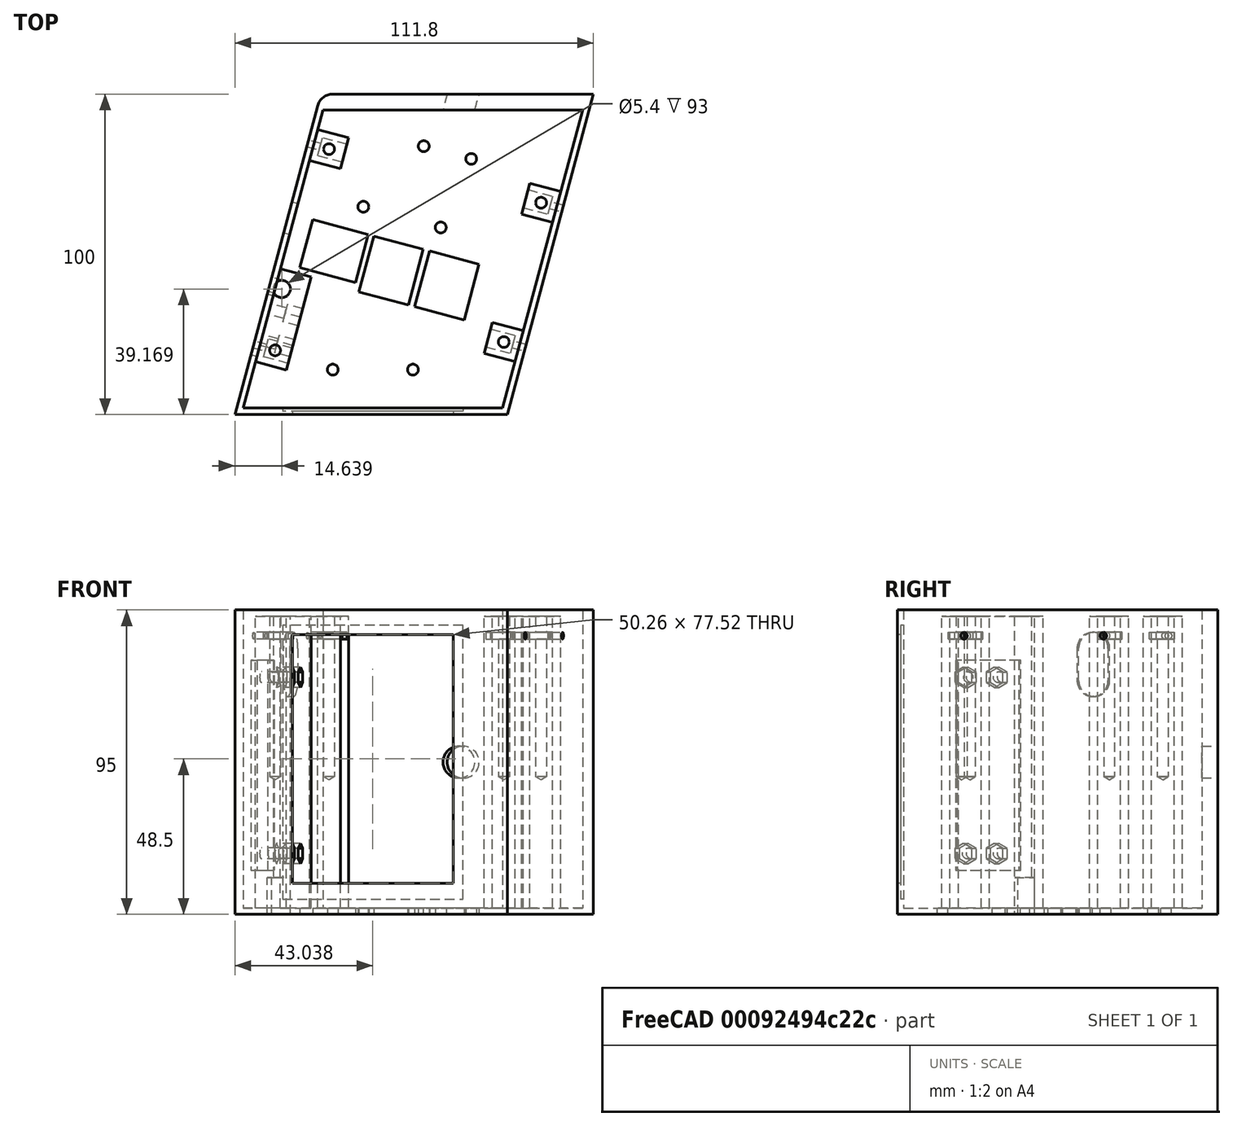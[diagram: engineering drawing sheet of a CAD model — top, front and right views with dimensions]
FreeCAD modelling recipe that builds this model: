
FCSTD DOCUMENT  (FreeCAD 0.21R33668 +26 (Git))
Label: Casing2
License: All rights reserved
LicenseURL: https://en.wikipedia.org/wiki/All_rights_reserved
objects: Sketcher::SketchObject×19, PartDesign::Pocket×14, PartDesign::CoordinateSystem×6, PartDesign::Hole×3, App::DocumentObjectGroup×3, PartDesign::Pad×2, Spreadsheet::Sheet×1, PartDesign::Fillet×1, App::FeaturePython×1, PartDesign::Body×1, App::Part×1, Mesh::Feature×1
note: 66 computed .brp shape members not serialized (recipe doc carries the construction recipe); baked Part::Feature solids carry a one-line shape summary decoded from their .brp
EXTERNAL_REF file=Display_Berrybase.FCStd obj=Spreadsheet
EXTERNAL_REF file=MLX90640.FCStd obj=Spreadsheet
EXTERNAL_REF file=Raspberrypi4B.FCStd obj=Spreadsheet
EXTERNAL_REF file=Support_Display_new.FCStd obj=Spreadsheet
EXTERNAL_REF file=Support_MLX.FCStd obj=Spreadsheet
EXTERNAL_REF file=Support_Raspi_new.FCStd obj=Spreadsheet

FEATURE [Spreadsheet::Sheet] Spreadsheet
  cells = B2='slant; C2(slant)==15 °; E2='main_case_width; F2(main_case_width)==95 mm; H2='display_width; I2(display_width)==<<Display_Berrybase>>#Spreadsheet.width; B3='walls_thickness; C3(walls_thickness)==2 mm; E3='main_case_height; F3(main_case_height)==85 mm; H3='display_height; I3(display_height)==<<Display_Berrybase>>#Spreadsheet.height; B4='screw_radius; C4(screw_radius)==1.5 mm; E4='main_case_length; F4(main_case_length)==100 mm; B5='front_thickness; C5(front_thickness)==5 mm; H5='mlx_cam_height; I5(mlx_cam_height)==<<MLX90640>>#Spreadsheet.cam_height; H6='mlx_extra_space; I6(mlx_extra_space)==2 mm; H7='mlx_radius; I7(mlx_radius)==<<MLX90640>>#Spreadsheet.cam_rad; B9='display_guard_depth; C9(display_guard_depth)==1 mm; E9='mlx_carrier_height; F9(mlx_carrier_height)==<<Support_MLX>>#Spreadsheet.carrier_height; H9='raspi_carrier_hole_dist; I9(raspi_carrier_hole_dist)==<<Support_Raspi_new>>#<<Spreadsheet>>.carrier_holes_space; B10='display_guard_size; C10(display_guard_size)==3 mm; E10='mlx_carrier_width; F10(mlx_carrier_width)==<<Support_MLX>>#Spreadsheet.carrier_width; H10='raspi_carrier_height; I10(raspi_carrier_height)==<<Support_Raspi_new>>#Spreadsheet.height; B11='display_clearance; C11(display_clearance)==1 mm; H11='raspi_carrier_depth; I11(raspi_carrier_depth)==<<Support_Raspi_new>>#Spreadsheet.depth; B12='display_hole_depth; C12(display_hole_depth)==display_width + display_clearance - display_guard_size - display_right_guard_extra; E12='beams_width; F12(beams_width)==10 mm; B13='display_right_guard_extra; C13(display_right_guard_extra)==5 mm; E13='beams_height; F13(beams_height)==10 mm; H13='raspi_height; I13(raspi_height)==<<Raspberrypi4B>>#Spreadsheet.height; H14='raspi_thickness; I14(raspi_thickness)==<<Raspberrypi4B>>#Spreadsheet.thickness; B15='display_thickness; C15(display_thickness)==<<Display_Berrybase>>#Spreadsheet.thickness; E15='beam_LB_offset; F15(beam_LB_offset)==80 mm; B16='display_carrier_height; C16(display_carrier_height)==<<Support_Display_new>>#Spreadsheet.height; E16='beam_LF_offset; F16(beam_LF_offset)==15 mm; H16='raspi_usb_width; I16(raspi_usb_width)==14 mm; E17='beam_UB_offset; F17(beam_UB_offset)==60 mm; H17='raspi_usb_height; I17(raspi_usb_height)==<<Raspberrypi4B>>#Spreadsheet.usb_height + 0 mm; B18='display_carrier_hole_dist; C18(display_carrier_hole_dist)==<<Support_Display_new>>#<<Spreadsheet>>.beams_seperation + <<Support_Display_new>>#<<Spreadsheet>>.beams_width; E18='beam_UF_offset; F18(beam_UF_offset)==15 mm; H18='raspi_eth_width; I18(raspi_eth_width)==<<Raspberrypi4B>>#Spreadsheet.ethernet_width; B19='display_carrier_offset; C19(display_carrier_offset)==display_thickness + display_carrier_height / 2 + 1 mm; H19='raspi_eth_height; I19(raspi_eth_height)==<<Raspberrypi4B>>#Spreadsheet.ethernet_height; E20='interface_width; F20(interface_width)==65 mm; H20='raspi_usb_lower_offset; I20(raspi_usb_lower_offset)==<<Raspberrypi4B>>#Spreadsheet.usb_lower_offset; B21='ports_clearance; C21(ports_clearance)==2 mm; E21='interface_height; F21(interface_height)==20 mm; H21='raspi_usb_middle_offset; I21(raspi_usb_middle_offset)==<<Raspberrypi4B>>#Spreadsheet.usb_middle_offset; E22='interface_screws_width; F22(interface_screws_width)==interface_width - beams_width; H22='raspi_eth_offset; I22(raspi_eth_offset)==<<Raspberrypi4B>>#Spreadsheet.ethernet_offset; B23='pen_radius; C23(pen_radius)==2.5 mm; E23='interface_screws_height; F23(interface_screws_height)==interface_height - beams_width; B24='pen_length; C24(pen_length)==90 mm; E24='interface_offset; F24(interface_offset)==2 mm; H24='sq_nut_width; I24(sq_nut_width)==5.8 mm; B25='pen_grip_width; C25(pen_grip_width)==7.5 mm; E25='interface_clearance; F25(interface_clearance)==0.5 mm; H25='sq_nut_height; I25(sq_nut_height)==2.1 mm; B26='pen_grip_height; C26(pen_grip_height)==11.5 mm; H26='sq_nut_hole_depth; I26(sq_nut_hole_depth)==(beams_height + sq_nut_width) / 2; B27='pen_radius_tolerance; C27(pen_radius_tolerance)==0.2 mm; H27='sq_nut_hole_offset; I27(sq_nut_hole_offset)==5 mm; B28='pen_hole_offset; C28(pen_hole_offset)==pen_grip_width - pen_radius - 1 mm
FEATURE [Sketcher::SketchObject] Sketch
  FullyConstrained = true
  MapMode = 5
  Support = -> [XY_Plane]
  expr: Constraints[7] = 90 ° + Spreadsheet.slant
  expr: Constraints[8] = Spreadsheet.main_case_height
  expr: Constraints[9] = Spreadsheet.main_case_length
  sketch-geometry (4):
    g0: LineSegment StartX=-29.1025 StartY=50 StartZ=0 EndX=55.8975 EndY=50 EndZ=0
    g1: LineSegment StartX=55.8975 StartY=50 StartZ=0 EndX=29.1025 EndY=-50 EndZ=0
    g2: LineSegment StartX=29.1025 StartY=-50 StartZ=0 EndX=-55.8975 EndY=-50 EndZ=0
    g3: LineSegment StartX=-55.8975 StartY=-50 StartZ=0 EndX=-29.1025 EndY=50 EndZ=0
  constraints (10):
    c: Coincident(g0,g1)
    c: Coincident(g1,g2)
    c: Coincident(g2,g3)
    c: Coincident(g3,g0)
    c: Horizontal(g0)
    c: Symmetric(g0,g2,g-1)
    c: Symmetric(g0,g1,g-1)
    c: Angle(g1,g2) = 1.8326
    c: DistanceX(g2,g2) = 85
    c: DistanceY(g1,g1) = 100
FEATURE [PartDesign::Pad] Pad
  Direction = (0,0,1)
  Length = 95
  Length2 = 10
  Profile = -> Sketch
  ReferenceAxis = -> Sketch [N_Axis]
  Type = 0
  expr: Length = Spreadsheet.main_case_width
FEATURE [Sketcher::SketchObject] Sketch001
  ExternalGeometry = -> [Pad]
  FullyConstrained = true
  MapMode = 5
  Placement = pos=(0,0,95) rot=(0,0,1;0rad)
  Support = -> [Pad]
  expr: Constraints[4] = Spreadsheet.walls_thickness
  expr: Constraints[5] = Spreadsheet.walls_thickness * (1 - tan(Spreadsheet.slant))
  expr: Constraints[7] = Spreadsheet.main_case_height - Spreadsheet.walls_thickness * 2
  expr: Constraints[8] = Spreadsheet.front_thickness
  sketch-geometry (4):
    g0: LineSegment StartX=-28.4423 StartY=45 StartZ=0 EndX=52.5577 EndY=45 EndZ=0
    g1: LineSegment StartX=52.5577 StartY=45 StartZ=0 EndX=27.6384 EndY=-48 EndZ=0
    g2: LineSegment StartX=27.6384 StartY=-48 StartZ=0 EndX=-53.3616 EndY=-48 EndZ=0
    g3: LineSegment StartX=-53.3616 StartY=-48 StartZ=0 EndX=-28.4423 EndY=45 EndZ=0
  constraints (12):
    c: Coincident(g0,g1)
    c: Coincident(g1,g2)
    c: Coincident(g2,g3)
    c: Coincident(g3,g0)
    c: DistanceY(g-5,g2) = 2
    c: DistanceX(g1,g-6) = 1.4641
    c: Horizontal(g2)
    c: DistanceX(g2,g2) = 81
    c: DistanceY(g0,g-4) = 5
    c: Horizontal(g0)
    c: Parallel(g3,g-4)
    c: Parallel(g1,g-6)
FEATURE [PartDesign::Pocket] Pocket
  BaseFeature = -> Pad
  Direction = (0,0,-1)
  Length = 93
  Length2 = 5
  Profile = -> Sketch001
  ReferenceAxis = -> Sketch001 [N_Axis]
  Type = 0
  expr: Length = Spreadsheet.main_case_width - Spreadsheet.walls_thickness
FEATURE [Sketcher::SketchObject] Sketch002
  ExternalGeometry = -> [Pocket]
  FullyConstrained = true
  MapMode = 5
  Placement = pos=(0,-48,0) rot=(0,0.707107,0.707107;3.14159rad)
  Support = -> [Pocket]
  expr: Constraints[11] = (Spreadsheet.main_case_width - Spreadsheet.walls_thickness * 2) / 2
  expr: Constraints[13] = Spreadsheet.display_width + Spreadsheet.display_clearance
  expr: Constraints[14] = Spreadsheet.display_height + Spreadsheet.display_clearance
  sketch-geometry (6):
    g0: LineSegment StartX=40.9916 StartY=4.74 StartZ=0 EndX=-15.2684 EndY=4.74 EndZ=0
    g1: LineSegment StartX=-15.2684 StartY=4.74 StartZ=0 EndX=-15.2684 EndY=90.26 EndZ=0
    g2: LineSegment StartX=-15.2684 StartY=90.26 StartZ=0 EndX=40.9916 EndY=90.26 EndZ=0
    g3: LineSegment StartX=40.9916 StartY=90.26 StartZ=0 EndX=40.9916 EndY=4.74 EndZ=0
    g4: LineSegment StartX=12.8616 StartY=95 StartZ=0 EndX=12.8616 EndY=2 EndZ=0
    g5: GeomPoint X=12.8616 Y=47.5 Z=0
  constraints (15):
    c: Coincident(g0,g1)
    c: Coincident(g1,g2)
    c: Coincident(g2,g3)
    c: Coincident(g3,g0)
    c: Horizontal(g0)
    c: Horizontal(g2)
    c: Vertical(g1)
    c: Vertical(g3)
    c: Symmetric(g-6,g-6,g4)
    c: Symmetric(g-5,g-4,g4)
    c: PointOnObject(g5,g4)
    c: DistanceY(g4,g5) = 45.5
    c: Symmetric(g1,g0,g5)
    c: DistanceY(g1,g1) = 85.52
    c: DistanceX(g2,g2) = 56.26
FEATURE [PartDesign::Pocket] Pocket001
  BaseFeature = -> Pocket
  Direction = (0,-1,2e-16)
  Length = 1
  Length2 = 5
  Profile = -> Sketch002
  ReferenceAxis = -> Sketch002 [N_Axis]
  Type = 0
  expr: Length = Spreadsheet.walls_thickness - Spreadsheet.display_guard_depth
FEATURE [Sketcher::SketchObject] Sketch003
  ExternalGeometry = -> [Pocket001]
  FullyConstrained = true
  MapMode = 5
  Placement = pos=(0,-49,1.23e-14) rot=(0,0.707107,0.707107;3.14159rad)
  Support = -> [Pocket001]
  expr: Constraints[10] = Spreadsheet.display_guard_size
  expr: Constraints[11] = Spreadsheet.display_guard_size
  expr: Constraints[8] = Spreadsheet.display_right_guard_extra
  expr: Constraints[9] = Spreadsheet.display_guard_size
  sketch-geometry (4):
    g0: LineSegment StartX=-12.2684 StartY=87.26 StartZ=0 EndX=37.9916 EndY=87.26 EndZ=0
    g1: LineSegment StartX=37.9916 StartY=87.26 StartZ=0 EndX=37.9916 EndY=9.74 EndZ=0
    g2: LineSegment StartX=37.9916 StartY=9.74 StartZ=0 EndX=-12.2684 EndY=9.74 EndZ=0
    g3: LineSegment StartX=-12.2684 StartY=9.74 StartZ=0 EndX=-12.2684 EndY=87.26 EndZ=0
  constraints (12):
    c: Coincident(g0,g1)
    c: Coincident(g1,g2)
    c: Coincident(g2,g3)
    c: Coincident(g3,g0)
    c: Horizontal(g0)
    c: Horizontal(g2)
    c: Vertical(g1)
    c: Vertical(g3)
    c: DistanceY(g-5,g2) = 5
    c: DistanceY(g0,g-5) = 3
    c: DistanceX(g-5,g0) = 3
    c: DistanceX(g0,g-4) = 3
FEATURE [PartDesign::Pocket] Pocket002
  BaseFeature = -> Pocket001
  Direction = (0,-1,2e-16)
  Length = 1
  Length2 = 5
  Profile = -> Sketch003
  ReferenceAxis = -> Sketch003 [N_Axis]
  Type = 0
  expr: Length = Spreadsheet.display_guard_depth
FEATURE [PartDesign::Fillet] Fillet
  Base = -> Pocket002 [Edge1]
  BaseFeature = -> Pocket002
  Radius = 5
  SupportTransform = false
  UseAllEdges = false
FEATURE [Sketcher::SketchObject] Sketch004
  ExternalGeometry = -> [Fillet]
  FullyConstrained = true
  MapMode = 5
  Placement = pos=(0,0,2) rot=(0,0,1;0rad)
  Support = -> [Fillet]
  expr: Constraints[10] = Spreadsheet.display_carrier_offset
  expr: Constraints[11] = Spreadsheet.display_carrier_hole_dist
  expr: Constraints[12] = Spreadsheet.screw_radius
  expr: Constraints[13] = Spreadsheet.screw_radius
  expr: Constraints[14] = Spreadsheet.screw_radius
  expr: Constraints[15] = Spreadsheet.screw_radius
  expr: Constraints[21] = Spreadsheet.raspi_carrier_height
  expr: Constraints[22] = Spreadsheet.walls_thickness
  expr: Constraints[25] = Spreadsheet.raspi_carrier_hole_dist
  expr: Constraints[26] = Spreadsheet.screw_radius
  expr: Constraints[27] = Spreadsheet.screw_radius
  expr: Constraints[30] = Spreadsheet.mlx_carrier_height - Spreadsheet.mlx_carrier_width
  expr: Constraints[33] = 90 ° + Spreadsheet.slant
  expr: Constraints[9] = Spreadsheet.mlx_cam_height + Spreadsheet.mlx_extra_space + Spreadsheet.front_thickness
  sketch-geometry (14):
    g0: Circle CenterX=3.02671 CenterY=33.7326 CenterZ=0 NormalX=0 NormalY=0 NormalZ=1 AngleXU=0 Radius=1.5
    g1: Circle CenterX=17.8247 CenterY=29.7674 CenterZ=0 NormalX=0 NormalY=0 NormalZ=1 AngleXU=0 Radius=1.5
    g2: Circle CenterX=-15.8225 CenterY=14.8236 CenterZ=0 NormalX=0 NormalY=0 NormalZ=1 AngleXU=0 Radius=1.5
    g3: Circle CenterX=8.32565 CenterY=8.35314 CenterZ=0 NormalX=0 NormalY=0 NormalZ=1 AngleXU=0 Radius=1.5
    g4: Circle CenterX=-25.3616 CenterY=-36 CenterZ=0 NormalX=0 NormalY=0 NormalZ=1 AngleXU=0 Radius=1.5
    g5: Circle CenterX=-0.361561 CenterY=-36 CenterZ=0 NormalX=0 NormalY=0 NormalZ=1 AngleXU=0 Radius=1.5
    g6: LineSegment StartX=15.3158 StartY=50 StartZ=0 EndX=10.4257 EndY=31.75 EndZ=0
    g7: LineSegment StartX=3.02671 StartY=33.7326 StartZ=0 EndX=17.8247 EndY=29.7674 EndZ=0
    g8: LineSegment StartX=-12.8616 StartY=-48 StartZ=0 EndX=-12.8616 EndY=-36 EndZ=0
    g9: LineSegment StartX=-25.3616 StartY=-36 StartZ=0 EndX=-0.361561 EndY=-36 EndZ=0
    g10: LineSegment StartX=-35.141 StartY=20 StartZ=0 EndX=25.7123 EndY=3.6944 EndZ=0
    g11: GeomPoint X=-33.2092 Y=19.4824 Z=0
    g12: GeomPoint X=-3.74843 Y=11.5884 Z=0
    g13: LineSegment StartX=-25.2659 StartY=50 StartZ=0 EndX=55.8975 EndY=50 EndZ=0
  constraints (34):
    c: Symmetric(g7,g7,g6)
    c: Coincident(g0,g7)
    c: Coincident(g1,g7)
    c: Symmetric(g-5,g-6,g8)
    c: Symmetric(g9,g9,g8)
    c: Coincident(g4,g9)
    c: Coincident(g5,g9)
    c: Vertical(g8)
    c: Horizontal(g9)
    c: DistanceY(g6,g6) = 18.25
    c: DistanceY(g8,g8) = 12
    c: DistanceX(g9,g9) = 25
    c: Radius(g0) = 1.5
    c: Radius(g1) = 1.5
    c: Radius(g4) = 1.5
    c: Radius(g5) = 1.5
    c: PointOnObject(g10,g-4)
    c: PointOnObject(g11,g10)
    c: Symmetric(g11,g10,g12)
    c: Perpendicular(g10,g-4)
    c: DistanceY(g10,g-4) = 25
    c: Distance(g11,g10) = 61
    c: Distance(g11,g10) = 2
    c: Symmetric(g2,g3,g12)
    c: PointOnObject(g2,g10)
    c: Distance(g3,g2) = 25
    c: Radius(g2) = 1.5
    c: Radius(g3) = 1.5
    c: Symmetric(g-7,g-8,g6)
    c: Perpendicular(g7,g6)
    c: Distance(g7) = 15.32
    c: Coincident(g13,g-7)
    c: Coincident(g13,g-8)
    c: Angle(g6,g13) = 1.8326
FEATURE [PartDesign::Hole] Hole
  BaseFeature = -> Fillet
  CustomThreadClearance = 0
  Depth = 358.646
  DepthType = 1
  Diameter = 3.4
  DrillForDepth = false
  DrillPoint = 1
  DrillPointAngle = 118
  HoleCutCountersinkAngle = 90
  HoleCutCustomValues = false
  HoleCutDepth = 0
  HoleCutDiameter = 6.1
  HoleCutType = 0
  ModelThread = false
  Profile = -> Sketch004
  Tapered = false
  TaperedAngle = 90
  ThreadClass = 0
  ThreadDepth = 358.646
  ThreadDepthType = 0
  ThreadDirection = 0
  ThreadFit = 0
  ThreadSize = 9
  ThreadType = 1
  Threaded = false
  UseCustomThreadClearance = false
FEATURE [Sketcher::SketchObject] Sketch005
  ExternalGeometry = -> [Hole]
  FullyConstrained = true
  MapMode = 5
  Placement = pos=(0,50,0) rot=(0,0.707107,0.707107;3.14159rad)
  Support = -> [Hole]
  expr: Constraints[2] = (Spreadsheet.mlx_radius + 0.15 mm) / cos(Spreadsheet.slant)
  sketch-geometry (3):
    g0: LineSegment StartX=-55.8975 StartY=95 StartZ=0 EndX=25.2659 EndY=0 EndZ=0
    g1: LineSegment StartX=-55.8975 StartY=0 StartZ=0 EndX=25.2659 EndY=95 EndZ=0
    g2: Circle CenterX=-15.3158 CenterY=47.5 CenterZ=0 NormalX=0 NormalY=0 NormalZ=1 AngleXU=0 Radius=4.96933
  constraints (7):
    c: PointOnObject(g2,g0)
    c: PointOnObject(g2,g1)
    c: Radius(g2) = 4.96933
    c: Coincident(g0,g-3)
    c: Coincident(g1,g-4)
    c: Coincident(g0,g-4)
    c: Coincident(g1,g-3)
FEATURE [PartDesign::Pocket] Pocket003
  BaseFeature = -> Hole
  Direction = (-0.267949,-1,0)
  Length = 5
  Length2 = 5
  Profile = -> Sketch005
  ReferenceAxis = -> Sketch005 [N_Axis]
  Type = 0
  UseCustomVector = true
  expr: .Direction.x = tan(Spreadsheet.slant) * -1
  expr: Length = Spreadsheet.front_thickness
FEATURE [Sketcher::SketchObject] Sketch006
  ExternalGeometry = -> [Pocket003]
  FullyConstrained = true
  MapMode = 5
  Placement = pos=(0,0,2) rot=(0,0,1;0rad)
  Support = -> [Pocket003]
  expr: Constraints[14] = Spreadsheet.raspi_height
  expr: Constraints[15] = Spreadsheet.raspi_thickness
  expr: Constraints[19] = Spreadsheet.raspi_eth_offset
  expr: Constraints[20] = Spreadsheet.raspi_usb_middle_offset
  expr: Constraints[21] = Spreadsheet.raspi_usb_lower_offset
  expr: Constraints[49] = Spreadsheet.raspi_eth_width + Spreadsheet.ports_clearance
  expr: Constraints[4] = (Spreadsheet.raspi_carrier_depth - Spreadsheet.ports_clearance) / 2
  expr: Constraints[50] = Spreadsheet.raspi_usb_width + Spreadsheet.ports_clearance
  expr: Constraints[51] = Spreadsheet.raspi_usb_width + Spreadsheet.ports_clearance
  expr: Constraints[52] = Spreadsheet.raspi_eth_height + Spreadsheet.ports_clearance
  expr: Constraints[53] = Spreadsheet.raspi_usb_height + Spreadsheet.ports_clearance
  expr: Constraints[54] = Spreadsheet.raspi_usb_height + Spreadsheet.ports_clearance
  sketch-geometry (21):
    g0: LineSegment StartX=-15.8225 StartY=14.8236 StartZ=0 EndX=8.32565 EndY=8.35314 EndZ=0
    g1: LineSegment StartX=-3.74843 StartY=11.5884 StartZ=0 EndX=-4.7837 EndY=7.72468 EndZ=0
    g2: LineSegment StartX=22.2622 StartY=0.477744 StartZ=0 EndX=-31.8296 EndY=14.9716 EndZ=0
    g3: LineSegment StartX=-31.8296 StartY=14.9716 StartZ=0 EndX=-32.8649 EndY=11.1079 EndZ=0
    g4: LineSegment StartX=-32.8649 StartY=11.1079 StartZ=0 EndX=21.2269 EndY=-3.38596 EndZ=0
    g5: LineSegment StartX=21.2269 StartY=-3.38596 StartZ=0 EndX=22.2622 EndY=0.477744 EndZ=0
    g6: GeomPoint X=-22.9642 Y=8.45501 Z=0
    g7: GeomPoint X=-4.85305 Y=3.60216 Z=0
    g8: GeomPoint X=12.5336 Y=-1.05659 Z=0
    g9: LineSegment StartX=-31.6575 StartY=10.7844 StartZ=0 EndX=-14.2708 EndY=6.12564 EndZ=0
    g10: LineSegment StartX=-14.2708 StartY=6.12564 StartZ=0 EndX=-18.2825 EndY=-8.84621 EndZ=0
    g11: LineSegment StartX=-18.2825 StartY=-8.84621 StartZ=0 EndX=-35.6692 EndY=-4.18747 EndZ=0
    g12: LineSegment StartX=-35.6692 StartY=-4.18747 StartZ=0 EndX=-31.6575 EndY=10.7844 EndZ=0
    g13: LineSegment StartX=-12.5805 StartY=5.67271 StartZ=0 EndX=2.87435 EndY=1.5316 EndZ=0
    g14: LineSegment StartX=2.87435 StartY=1.5316 StartZ=0 EndX=-1.78439 EndY=-15.8551 EndZ=0
    g15: LineSegment StartX=-1.78439 StartY=-15.8551 StartZ=0 EndX=-17.2392 EndY=-11.714 EndZ=0
    g16: LineSegment StartX=-17.2392 StartY=-11.714 StartZ=0 EndX=-12.5805 EndY=5.67271 EndZ=0
    g17: LineSegment StartX=4.8062 StartY=1.01396 StartZ=0 EndX=20.261 EndY=-3.12714 EndZ=0
    g18: LineSegment StartX=20.261 StartY=-3.12714 StartZ=0 EndX=15.6023 EndY=-20.5138 EndZ=0
    g19: LineSegment StartX=15.6023 StartY=-20.5138 StartZ=0 EndX=0.147462 EndY=-16.3727 EndZ=0
    g20: LineSegment StartX=0.147462 StartY=-16.3727 StartZ=0 EndX=4.8062 EndY=1.01396 EndZ=0
  constraints (55):
    c: Coincident(g0,g-3)
    c: Coincident(g0,g-4)
    c: Symmetric(g0,g0,g1)
    c: Perpendicular(g1,g0)
    c: Distance(g1) = 4
    c: Coincident(g2,g3)
    c: Coincident(g3,g4)
    c: Coincident(g4,g5)
    c: Coincident(g5,g2)
    c: Symmetric(g2,g2,g1)
    c: Parallel(g0,g2)
    c: Parallel(g2,g4)
    c: Parallel(g1,g5)
    c: Parallel(g1,g3)
    c: Distance(g2) = 56
    c: Distance(g5) = 4
    c: PointOnObject(g6,g4)
    c: PointOnObject(g7,g4)
    c: PointOnObject(g8,g4)
    c: Distance(g6,g3) = 10.25
    c: Distance(g7,g3) = 29
    c: Distance(g8,g3) = 47
    c: Coincident(g9,g10)
    c: Coincident(g10,g11)
    c: Coincident(g11,g12)
    c: Coincident(g12,g9)
    c: Coincident(g13,g14)
    c: Coincident(g14,g15)
    c: Coincident(g15,g16)
    c: Coincident(g16,g13)
    c: Coincident(g17,g18)
    c: Coincident(g18,g19)
    c: Coincident(g19,g20)
    c: Coincident(g20,g17)
    c: PointOnObject(g9,g4)
    c: PointOnObject(g13,g4)
    c: PointOnObject(g17,g4)
    c: Symmetric(g9,g9,g6)
    c: Symmetric(g13,g13,g7)
    c: Symmetric(g17,g17,g8)
    c: Equal(g9,g11)
    c: Equal(g13,g15)
    c: Equal(g17,g19)
    c: Perpendicular(g12,g9)
    c: Perpendicular(g16,g13)
    c: Perpendicular(g20,g17)
    c: Parallel(g9,g11)
    c: Parallel(g13,g15)
    c: Parallel(g17,g19)
    c: Distance(g11) = 18
    c: Distance(g15) = 16
    c: Distance(g19) = 16
    c: Distance(g12) = 15.5
    c: Distance(g16) = 18
    c: Distance(g20) = 18
FEATURE [PartDesign::Pocket] Pocket004
  BaseFeature = -> Pocket003
  Direction = (0,0,-1)
  Length = 5
  Length2 = 5
  Profile = -> Sketch006
  ReferenceAxis = -> Sketch006 [N_Axis]
  Type = 1
FEATURE [Sketcher::SketchObject] Sketch007
  ExternalGeometry = -> [Pocket004]
  FullyConstrained = true
  MapMode = 5
  Placement = pos=(0,0,2) rot=(0,0,1;0rad)
  Support = -> [Pocket004]
  expr: Constraints[36] = Spreadsheet.beams_height
  expr: Constraints[37] = Spreadsheet.beams_height
  expr: Constraints[38] = Spreadsheet.beams_height
  expr: Constraints[39] = Spreadsheet.beams_height
  expr: Constraints[40] = Spreadsheet.beams_width
  expr: Constraints[41] = Spreadsheet.beams_width * 3
  expr: Constraints[42] = Spreadsheet.beams_width
  expr: Constraints[43] = Spreadsheet.beams_width
  expr: Constraints[44] = Spreadsheet.beam_LF_offset
  expr: Constraints[45] = Spreadsheet.beam_LB_offset
  expr: Constraints[46] = Spreadsheet.beam_UF_offset
  expr: Constraints[47] = Spreadsheet.beam_UB_offset
  sketch-geometry (16):
    g0: LineSegment StartX=-30.0678 StartY=38.9333 StartZ=0 EndX=-20.4086 EndY=36.3451 EndZ=0
    g1: LineSegment StartX=-20.4086 StartY=36.3451 StartZ=0 EndX=-22.9968 EndY=26.6859 EndZ=0
    g2: LineSegment StartX=-22.9968 StartY=26.6859 StartZ=0 EndX=-32.656 EndY=29.2741 EndZ=0
    g3: LineSegment StartX=-32.656 StartY=29.2741 StartZ=0 EndX=-30.0678 EndY=38.9333 EndZ=0
    g4: LineSegment StartX=-41.7147 StartY=-4.53334 StartZ=0 EndX=-32.0554 EndY=-7.12153 EndZ=0
    g5: LineSegment StartX=-32.0554 StartY=-7.12153 StartZ=0 EndX=-39.82 EndY=-36.0993 EndZ=0
    g6: LineSegment StartX=-39.82 StartY=-36.0993 StartZ=0 EndX=-49.4793 EndY=-33.5111 EndZ=0
    g7: LineSegment StartX=-49.4793 StartY=-33.5111 StartZ=0 EndX=-41.7147 EndY=-4.53334 EndZ=0
    g8: LineSegment StartX=24.4497 StartY=-21.2637 StartZ=0 EndX=34.1089 EndY=-23.8519 EndZ=0
    g9: LineSegment StartX=34.1089 StartY=-23.8519 StartZ=0 EndX=31.5207 EndY=-33.5111 EndZ=0
    g10: LineSegment StartX=31.5207 StartY=-33.5111 StartZ=0 EndX=21.8615 EndY=-30.9229 EndZ=0
    g11: LineSegment StartX=21.8615 StartY=-30.9229 StartZ=0 EndX=24.4497 EndY=-21.2637 EndZ=0
    g12: LineSegment StartX=36.0965 StartY=22.203 StartZ=0 EndX=45.7558 EndY=19.6148 EndZ=0
    g13: LineSegment StartX=45.7558 StartY=19.6148 StartZ=0 EndX=43.1676 EndY=9.95555 EndZ=0
    g14: LineSegment StartX=43.1676 StartY=9.95555 StartZ=0 EndX=33.5083 EndY=12.5437 EndZ=0
    g15: LineSegment StartX=33.5083 StartY=12.5437 StartZ=0 EndX=36.0965 EndY=22.203 EndZ=0
  constraints (48):
    c: Coincident(g0,g1)
    c: Coincident(g1,g2)
    c: Coincident(g2,g3)
    c: Coincident(g3,g0)
    c: Coincident(g4,g5)
    c: Coincident(g5,g6)
    c: Coincident(g6,g7)
    c: Coincident(g7,g4)
    c: Coincident(g8,g9)
    c: Coincident(g9,g10)
    c: Coincident(g10,g11)
    c: Coincident(g11,g8)
    c: Coincident(g12,g13)
    c: Coincident(g13,g14)
    c: Coincident(g14,g15)
    c: Coincident(g15,g12)
    c: PointOnObject(g0,g-3)
    c: PointOnObject(g2,g-3)
    c: PointOnObject(g4,g-3)
    c: PointOnObject(g6,g-3)
    c: PointOnObject(g12,g-4)
    c: PointOnObject(g13,g-4)
    c: PointOnObject(g8,g-4)
    c: PointOnObject(g9,g-4)
    c: Equal(g3,g1)
    c: Equal(g7,g5)
    c: Equal(g13,g15)
    c: Equal(g9,g11)
    c: Parallel(g3,g1)
    c: Parallel(g7,g5)
    c: Parallel(g9,g11)
    c: Parallel(g13,g15)
    c: Perpendicular(g0,g3)
    c: Perpendicular(g4,g7)
    c: Perpendicular(g12,g13)
    c: Perpendicular(g8,g9)
    c: Distance(g0) = 10
    c: Distance(g4) = 10
    c: Distance(g12) = 10
    c: Distance(g8) = 10
    c: Distance(g1) = 10
    c: Distance(g5) = 30
    c: Distance(g15) = 10
    c: Distance(g11) = 10
    c: Distance(g6,g-6) = 15
    c: Distance(g2,g-6) = 80
    c: Distance(g9,g-6) = 15
    c: Distance(g13,g-6) = 60
FEATURE [PartDesign::Pad] Pad001
  BaseFeature = -> Pocket004
  Direction = (0,0,1)
  Length = 91
  Length2 = 10
  Profile = -> Sketch007
  ReferenceAxis = -> Sketch007 [N_Axis]
  Type = 0
  expr: Length = Spreadsheet.main_case_width - Spreadsheet.walls_thickness * 2
FEATURE [Sketcher::SketchObject] Sketch008
  ExternalGeometry = -> [Pad001]
  FullyConstrained = true
  MapMode = 5
  Placement = pos=(0,0,93) rot=(0,0,1;0rad)
  Support = -> [Pad001]
  expr: Constraints[10] = Spreadsheet.beams_width
  expr: Constraints[3] = Spreadsheet.screw_radius
  expr: Constraints[4] = Spreadsheet.screw_radius
  expr: Constraints[5] = Spreadsheet.screw_radius
  expr: Constraints[6] = Spreadsheet.screw_radius
  sketch-geometry (5):
    g0: Circle CenterX=-26.5323 CenterY=32.8096 CenterZ=0 NormalX=0 NormalY=0 NormalZ=1 AngleXU=0 Radius=1.5
    g1: Circle CenterX=39.632 CenterY=16.0793 CenterZ=0 NormalX=0 NormalY=0 NormalZ=1 AngleXU=0 Radius=1.5
    g2: Circle CenterX=27.9852 CenterY=-27.3874 CenterZ=0 NormalX=0 NormalY=0 NormalZ=1 AngleXU=0 Radius=1.5
    g3: Circle CenterX=-43.3556 CenterY=-29.9756 CenterZ=0 NormalX=0 NormalY=0 NormalZ=1 AngleXU=0 Radius=1.5
    g4: LineSegment StartX=-37.2318 StartY=-26.44 StartZ=0 EndX=-46.8911 EndY=-23.8519 EndZ=0
  constraints (12):
    c: Symmetric(g-3,g-5,g0)
    c: Symmetric(g-7,g-8,g1)
    c: Symmetric(g-10,g-11,g2)
    c: Radius(g0) = 1.5
    c: Radius(g3) = 1.5
    c: Radius(g1) = 1.5
    c: Radius(g2) = 1.5
    c: PointOnObject(g4,g-13)
    c: PointOnObject(g4,g-15)
    c: Parallel(g4,g-14)
    c: Distance(g4,g-14) = 10
    c: Symmetric(g4,g-14,g3)
FEATURE [PartDesign::Hole] Hole001
  BaseFeature = -> Pad001
  CustomThreadClearance = 0
  Depth = 50
  DepthType = 0
  Diameter = 3.4
  DrillForDepth = false
  DrillPoint = 1
  DrillPointAngle = 118
  HoleCutCountersinkAngle = 90
  HoleCutCustomValues = false
  HoleCutDepth = 0
  HoleCutDiameter = 6.1
  HoleCutType = 0
  ModelThread = false
  Profile = -> Sketch008
  Tapered = false
  TaperedAngle = 90
  ThreadClass = 0
  ThreadDepth = 50
  ThreadDepthType = 0
  ThreadDirection = 0
  ThreadFit = 0
  ThreadSize = 9
  ThreadType = 1
  Threaded = false
  UseCustomThreadClearance = false
  expr: Depth = 50
FEATURE [Sketcher::SketchObject] Sketch009
  ExternalGeometry = -> [Hole001]
  FullyConstrained = true
  MapMode = 5
  Placement = pos=(28.1278,-7.53681,0) rot=(-0.476905,0.621515,0.621515;4.0316rad)
  Support = -> [Hole001]
  expr: Constraints[19] = Spreadsheet.sq_nut_hole_offset
  expr: Constraints[20] = Spreadsheet.sq_nut_height
  expr: Constraints[21] = Spreadsheet.sq_nut_width
  expr: Constraints[25] = Spreadsheet.sq_nut_hole_offset
  expr: Constraints[26] = Spreadsheet.sq_nut_height
  expr: Constraints[27] = Spreadsheet.sq_nut_width
  sketch-geometry (10):
    g0: LineSegment StartX=-28.6889 StartY=88 StartZ=0 EndX=-22.8889 EndY=88 EndZ=0
    g1: LineSegment StartX=-22.8889 StartY=88 StartZ=0 EndX=-22.8889 EndY=85.9 EndZ=0
    g2: LineSegment StartX=-22.8889 StartY=85.9 StartZ=0 EndX=-28.6889 EndY=85.9 EndZ=0
    g3: LineSegment StartX=-28.6889 StartY=85.9 StartZ=0 EndX=-28.6889 EndY=88 EndZ=0
    g4: LineSegment StartX=16.3111 StartY=88 StartZ=0 EndX=22.1111 EndY=88 EndZ=0
    g5: LineSegment StartX=22.1111 StartY=88 StartZ=0 EndX=22.1111 EndY=85.9 EndZ=0
    g6: LineSegment StartX=22.1111 StartY=85.9 StartZ=0 EndX=16.3111 EndY=85.9 EndZ=0
    g7: LineSegment StartX=16.3111 StartY=85.9 StartZ=0 EndX=16.3111 EndY=88 EndZ=0
    g8: LineSegment StartX=-25.7889 StartY=93 StartZ=0 EndX=-25.7889 EndY=88 EndZ=0
    g9: LineSegment StartX=19.2111 StartY=93 StartZ=0 EndX=19.2111 EndY=88 EndZ=0
  constraints (28):
    c: Coincident(g0,g1)
    c: Coincident(g1,g2)
    c: Coincident(g2,g3)
    c: Coincident(g3,g0)
    c: Horizontal(g0)
    c: Horizontal(g2)
    c: Vertical(g1)
    c: Vertical(g3)
    c: Coincident(g4,g5)
    c: Coincident(g5,g6)
    c: Coincident(g6,g7)
    c: Coincident(g7,g4)
    c: Horizontal(g4)
    c: Horizontal(g6)
    c: Vertical(g5)
    c: Vertical(g7)
    c: Vertical(g8)
    c: Symmetric(g-4,g-5,g8)
    c: Symmetric(g0,g0,g8)
    c: DistanceY(g8,g8) = 5
    c: DistanceY(g3,g3) = 2.1
    c: DistanceX(g2,g2) = 5.8
    c: Vertical(g9)
    c: Symmetric(g-7,g-8,g9)
    c: Symmetric(g4,g4,g9)
    c: DistanceY(g9,g9) = 5
    c: DistanceY(g7,g7) = 2.1
    c: DistanceX(g6,g6) = 5.8
FEATURE [PartDesign::Pocket] Pocket005
  BaseFeature = -> Hole001
  Direction = (0.965926,-0.258819,-2e-16)
  Length = 7.9
  Length2 = 5
  Profile = -> Sketch009
  ReferenceAxis = -> Sketch009 [N_Axis]
  Type = 0
  expr: Length = Spreadsheet.sq_nut_hole_depth
FEATURE [Sketcher::SketchObject] Sketch010
  ExternalGeometry = -> [Pocket005]
  FullyConstrained = true
  MapMode = 5
  Placement = pos=(-28.1278,7.53681,0) rot=(0.677661,0.519988,0.519988;1.95044rad)
  Support = -> [Pocket005]
  expr: Constraints[19] = Spreadsheet.sq_nut_hole_offset
  expr: Constraints[20] = Spreadsheet.sq_nut_height
  expr: Constraints[21] = Spreadsheet.sq_nut_width
  expr: Constraints[24] = Spreadsheet.sq_nut_hole_offset
  expr: Constraints[25] = Spreadsheet.sq_nut_height
  expr: Constraints[26] = Spreadsheet.sq_nut_width
  expr: Constraints[29] = Spreadsheet.beams_width
  sketch-geometry (11):
    g0: LineSegment StartX=-43.0754 StartY=88 StartZ=0 EndX=-37.2754 EndY=88 EndZ=0
    g1: LineSegment StartX=-37.2754 StartY=88 StartZ=0 EndX=-37.2754 EndY=85.9 EndZ=0
    g2: LineSegment StartX=-37.2754 StartY=85.9 StartZ=0 EndX=-43.0754 EndY=85.9 EndZ=0
    g3: LineSegment StartX=-43.0754 StartY=85.9 StartZ=0 EndX=-43.0754 EndY=88 EndZ=0
    g4: LineSegment StartX=21.9246 StartY=88 StartZ=0 EndX=27.7246 EndY=88 EndZ=0
    g5: LineSegment StartX=27.7246 StartY=88 StartZ=0 EndX=27.7246 EndY=85.9 EndZ=0
    g6: LineSegment StartX=27.7246 StartY=85.9 StartZ=0 EndX=21.9246 EndY=85.9 EndZ=0
    g7: LineSegment StartX=21.9246 StartY=85.9 StartZ=0 EndX=21.9246 EndY=88 EndZ=0
    g8: LineSegment StartX=-40.1754 StartY=93 StartZ=0 EndX=-40.1754 EndY=88 EndZ=0
    g9: LineSegment StartX=24.8246 StartY=93 StartZ=0 EndX=24.8246 EndY=88 EndZ=0
    g10: GeomPoint X=-35.1754 Y=93 Z=0
  constraints (30):
    c: Coincident(g0,g1)
    c: Coincident(g1,g2)
    c: Coincident(g2,g3)
    c: Coincident(g3,g0)
    c: Horizontal(g0)
    c: Horizontal(g2)
    c: Vertical(g1)
    c: Vertical(g3)
    c: Coincident(g4,g5)
    c: Coincident(g5,g6)
    c: Coincident(g6,g7)
    c: Coincident(g7,g4)
    c: Horizontal(g4)
    c: Horizontal(g6)
    c: Vertical(g5)
    c: Vertical(g7)
    c: Vertical(g9)
    c: Symmetric(g0,g0,g8)
    c: Vertical(g8)
    c: DistanceY(g8,g8) = 5
    c: DistanceY(g3,g3) = 2.1
    c: DistanceX(g2,g2) = 5.8
    c: Symmetric(g-7,g-8,g9)
    c: Symmetric(g4,g4,g9)
    c: DistanceY(g9,g9) = 5
    c: DistanceY(g7,g7) = 2.1
    c: DistanceX(g6,g6) = 5.8
    c: PointOnObject(g10,g-4)
    c: Symmetric(g-4,g10,g8)
    c: DistanceX(g-4,g10) = 10
FEATURE [PartDesign::Pocket] Pocket006
  BaseFeature = -> Pocket005
  Direction = (-0.965926,0.258819,1e-16)
  Length = 7.9
  Length2 = 5
  Profile = -> Sketch010
  ReferenceAxis = -> Sketch010 [N_Axis]
  Type = 0
  expr: Length = Spreadsheet.sq_nut_hole_depth
FEATURE [Sketcher::SketchObject] Sketch011
  ExternalGeometry = -> [Pocket006]
  FullyConstrained = true
  MapMode = 5
  Placement = pos=(-37.787,10.125,0) rot=(0.677661,0.519988,0.519988;1.95044rad)
  Support = -> [Pocket006]
  sketch-geometry (10):
    g0: LineSegment StartX=-4.17543 StartY=88 StartZ=0 EndX=5.82457 EndY=88 EndZ=0
    g1: LineSegment StartX=5.82457 StartY=88 StartZ=0 EndX=5.82457 EndY=68 EndZ=0
    g2: LineSegment StartX=5.82457 StartY=68 StartZ=0 EndX=-4.17543 EndY=68 EndZ=0
    g3: LineSegment StartX=-4.17543 StartY=68 StartZ=0 EndX=-4.17543 EndY=88 EndZ=0
    g4: LineSegment StartX=-4.17543 StartY=83 StartZ=0 EndX=-4.17543 EndY=73 EndZ=0
    g5: LineSegment StartX=5.82457 StartY=83 StartZ=0 EndX=5.82457 EndY=73 EndZ=0
    g6: ArcOfCircle CenterX=0.824572 CenterY=83 CenterZ=0 NormalX=0 NormalY=0 NormalZ=1 AngleXU=0 Radius=5 StartAngle=-3.6e-15 EndAngle=3.14159
    g7: ArcOfCircle CenterX=0.824572 CenterY=73 CenterZ=0 NormalX=0 NormalY=0 NormalZ=1 AngleXU=0 Radius=5 StartAngle=3.14159 EndAngle=6.28319
    g8: LineSegment StartX=-4.17543 StartY=83 StartZ=0 EndX=5.82457 EndY=83 EndZ=0
    g9: LineSegment StartX=-4.17543 StartY=73 StartZ=0 EndX=5.82457 EndY=73 EndZ=0
  constraints (30):
    c: Coincident(g0,g1)
    c: Coincident(g1,g2)
    c: Coincident(g2,g3)
    c: Coincident(g3,g0)
    c: Horizontal(g0)
    c: Horizontal(g2)
    c: Vertical(g1)
    c: Vertical(g3)
    c: DistanceX(g0,g0) = 10
    c: DistanceY(g3,g3) = 20
    c: PointOnObject(g4,g3)
    c: PointOnObject(g4,g3)
    c: PointOnObject(g5,g1)
    c: PointOnObject(g5,g1)
    c: Coincident(g6,g4)
    c: Coincident(g6,g5)
    c: Coincident(g7,g4)
    c: Coincident(g7,g5)
    c: Tangent(g6,g0)
    c: Tangent(g7,g2)
    c: Coincident(g8,g4)
    c: Coincident(g8,g5)
    c: Horizontal(g8)
    c: Coincident(g9,g4)
    c: Coincident(g9,g5)
    c: PointOnObject(g6,g8)
    c: PointOnObject(g7,g9)
    c: Horizontal(g9)
    c: DistanceY(g0,g-4) = 5
    c: DistanceX(g0,g-4) = 14
FEATURE [PartDesign::Pocket] Pocket007
  BaseFeature = -> Pocket006
  Direction = (-0.965926,0.258819,2e-16)
  Length = 5
  Length2 = 5
  Profile = -> Sketch011
  ReferenceAxis = -> Sketch011 [N_Axis]
  Type = 1
FEATURE [App::DocumentObjectGroup] Parts
FEATURE [PartDesign::CoordinateSystem] LCS_Origin
  AttacherType = Attacher::AttachEngine3D
  MapMode = 2
  Support = -> [X_Axis001]
FEATURE [App::DocumentObjectGroup] Constraints
FEATURE [App::FeaturePython] Variables  # WARN: FeaturePython — macro-defined, semantics opaque (R4)
  Type = App::PropertyContainer
FEATURE [App::DocumentObjectGroup] Configurations
FEATURE [PartDesign::CoordinateSystem] LCS_MLX
  AttacherType = Attacher::AttachEngine3D
  AttachmentOffset = pos=(0,0,0) rot=(0,0,-1;0.261799rad)
  MapMode = 11
  Placement = pos=(17.8247,29.7674,2) rot=(0,0,1;1.309rad)
  Support = -> [Hole]
  expr: .AttachmentOffset.Rotation.Yaw = Spreadsheet.slant * -1
FEATURE [PartDesign::CoordinateSystem] LCS_Raspi
  AttacherType = Attacher::AttachEngine3D
  AttachmentOffset = pos=(0,0,0) rot=(0,0,-1;0.261799rad)
  MapMode = 11
  Placement = pos=(8.32565,8.35314,2) rot=(0,0,1;1.309rad)
  Support = -> [Hole]
  expr: .AttachmentOffset.Rotation.Yaw = Spreadsheet.slant * -1
FEATURE [PartDesign::CoordinateSystem] LCS_Display
  AttacherType = Attacher::AttachEngine3D
  MapMode = 11
  Placement = pos=(-0.361561,-36,2) rot=(0,0,1;1.5708rad)
  Support = -> [Hole]
FEATURE [PartDesign::CoordinateSystem] LCS_beam
  AttacherType = Attacher::AttachEngine3D
  MapMode = 11
  Placement = pos=(-26.5323,32.8096,93) rot=(0,0,1;1.5708rad)
  Support = -> [Hole001]
FEATURE [Sketcher::SketchObject] Sketch012
  ExternalGeometry = -> [Pocket007]
  FullyConstrained = true
  MapMode = 5
  Placement = pos=(-28.1278,7.53681,0) rot=(0.677661,0.519988,0.519988;1.95044rad)
  Support = -> [Pocket007]
  expr: Constraints[12] = Spreadsheet.interface_screws_width
  expr: Constraints[13] = Spreadsheet.interface_screws_height
  expr: Constraints[18] = Spreadsheet.beams_width + Spreadsheet.interface_offset
  expr: Constraints[20] = Spreadsheet.screw_radius
  expr: Constraints[21] = Spreadsheet.screw_radius
  expr: Constraints[22] = Spreadsheet.screw_radius
  expr: Constraints[23] = Spreadsheet.screw_radius
  sketch-geometry (10):
    g0: Circle CenterX=-38.1754 CenterY=74 CenterZ=0 NormalX=0 NormalY=0 NormalZ=1 AngleXU=0 Radius=1.5
    g1: Circle CenterX=-38.1754 CenterY=19 CenterZ=0 NormalX=0 NormalY=0 NormalZ=1 AngleXU=0 Radius=1.5
    g2: Circle CenterX=-28.1754 CenterY=19 CenterZ=0 NormalX=0 NormalY=0 NormalZ=1 AngleXU=0 Radius=1.5
    g3: Circle CenterX=-28.1754 CenterY=74 CenterZ=0 NormalX=0 NormalY=0 NormalZ=1 AngleXU=0 Radius=1.5
    g4: LineSegment StartX=-38.1754 StartY=74 StartZ=0 EndX=-28.1754 EndY=74 EndZ=0
    g5: LineSegment StartX=-28.1754 StartY=74 StartZ=0 EndX=-28.1754 EndY=19 EndZ=0
    g6: LineSegment StartX=-28.1754 StartY=19 StartZ=0 EndX=-38.1754 EndY=19 EndZ=0
    g7: LineSegment StartX=-38.1754 StartY=19 StartZ=0 EndX=-38.1754 EndY=74 EndZ=0
    g8: LineSegment StartX=-33.1754 StartY=93 StartZ=0 EndX=-33.1754 EndY=0 EndZ=0
    g9: GeomPoint X=-33.1754 Y=46.5 Z=0
  constraints (24):
    c: Coincident(g4,g5)
    c: Coincident(g5,g6)
    c: Coincident(g6,g7)
    c: Coincident(g7,g4)
    c: Horizontal(g4)
    c: Horizontal(g6)
    c: Vertical(g5)
    c: Vertical(g7)
    c: Coincident(g0,g4)
    c: Coincident(g3,g4)
    c: Coincident(g1,g6)
    c: Coincident(g2,g5)
    c: DistanceY(g5,g5) = 55
    c: DistanceX(g4,g4) = 10
    c: PointOnObject(g8,g-3)
    c: PointOnObject(g8,g-1)
    c: Symmetric(g8,g8,g9)
    c: Vertical(g8)
    c: DistanceX(g-4,g8) = 12
    c: Symmetric(g0,g2,g9)
    c: Radius(g0) = 1.5
    c: Radius(g3) = 1.5
    c: Radius(g1) = 1.5
    c: Radius(g2) = 1.5
FEATURE [PartDesign::Hole] Hole002
  BaseFeature = -> Pocket007
  CustomThreadClearance = 0
  Depth = 358.646
  DepthType = 1
  Diameter = 3.4
  DrillForDepth = false
  DrillPoint = 1
  DrillPointAngle = 118
  HoleCutCountersinkAngle = 90
  HoleCutCustomValues = false
  HoleCutDepth = 0
  HoleCutDiameter = 6.1
  HoleCutType = 0
  ModelThread = false
  Profile = -> Sketch012
  Tapered = false
  TaperedAngle = 90
  ThreadClass = 0
  ThreadDepth = 358.646
  ThreadDepthType = 0
  ThreadDirection = 0
  ThreadFit = 0
  ThreadSize = 9
  ThreadType = 1
  Threaded = false
  UseCustomThreadClearance = false
FEATURE [Sketcher::SketchObject] Sketch013
  ExternalGeometry = -> [Hole002]
  FullyConstrained = true
  MapMode = 5
  Placement = pos=(-28.1278,7.53681,0) rot=(0.677661,0.519988,0.519988;1.95044rad)
  Support = -> [Hole002]
  sketch-geometry (28):
    g0: LineSegment StartX=-35.4254 StartY=75.5877 StartZ=0 EndX=-38.1754 EndY=77.1754 EndZ=0
    g1: LineSegment StartX=-38.1754 StartY=77.1754 StartZ=0 EndX=-40.9254 EndY=75.5877 EndZ=0
    g2: LineSegment StartX=-40.9254 StartY=75.5877 StartZ=0 EndX=-40.9254 EndY=72.4123 EndZ=0
    g3: LineSegment StartX=-40.9254 StartY=72.4123 StartZ=0 EndX=-38.1754 EndY=70.8246 EndZ=0
    g4: LineSegment StartX=-38.1754 StartY=70.8246 StartZ=0 EndX=-35.4254 EndY=72.4123 EndZ=0
    g5: LineSegment StartX=-35.4254 StartY=72.4123 StartZ=0 EndX=-35.4254 EndY=75.5877 EndZ=0
    g6: Circle CenterX=-38.1754 CenterY=74 CenterZ=0 NormalX=0 NormalY=0 NormalZ=1 AngleXU=0 Radius=3.17543
    g7: LineSegment StartX=-25.4254 StartY=75.5877 StartZ=0 EndX=-28.1754 EndY=77.1754 EndZ=0
    g8: LineSegment StartX=-28.1754 StartY=77.1754 StartZ=0 EndX=-30.9254 EndY=75.5877 EndZ=0
    g9: LineSegment StartX=-30.9254 StartY=75.5877 StartZ=0 EndX=-30.9254 EndY=72.4123 EndZ=0
    g10: LineSegment StartX=-30.9254 StartY=72.4123 StartZ=0 EndX=-28.1754 EndY=70.8246 EndZ=0
    g11: LineSegment StartX=-28.1754 StartY=70.8246 StartZ=0 EndX=-25.4254 EndY=72.4123 EndZ=0
    g12: LineSegment StartX=-25.4254 StartY=72.4123 StartZ=0 EndX=-25.4254 EndY=75.5877 EndZ=0
    g13: Circle CenterX=-28.1754 CenterY=74 CenterZ=0 NormalX=0 NormalY=0 NormalZ=1 AngleXU=0 Radius=3.17543
    g14: LineSegment StartX=-35.4254 StartY=20.5877 StartZ=0 EndX=-38.1754 EndY=22.1754 EndZ=0
    g15: LineSegment StartX=-38.1754 StartY=22.1754 StartZ=0 EndX=-40.9254 EndY=20.5877 EndZ=0
    g16: LineSegment StartX=-40.9254 StartY=20.5877 StartZ=0 EndX=-40.9254 EndY=17.4123 EndZ=0
    g17: LineSegment StartX=-40.9254 StartY=17.4123 StartZ=0 EndX=-38.1754 EndY=15.8246 EndZ=0
    g18: LineSegment StartX=-38.1754 StartY=15.8246 StartZ=0 EndX=-35.4254 EndY=17.4123 EndZ=0
    g19: LineSegment StartX=-35.4254 StartY=17.4123 StartZ=0 EndX=-35.4254 EndY=20.5877 EndZ=0
    g20: Circle CenterX=-38.1754 CenterY=19 CenterZ=0 NormalX=0 NormalY=0 NormalZ=1 AngleXU=0 Radius=3.17543
    g21: LineSegment StartX=-25.4254 StartY=20.5877 StartZ=0 EndX=-28.1754 EndY=22.1754 EndZ=0
    g22: LineSegment StartX=-28.1754 StartY=22.1754 StartZ=0 EndX=-30.9254 EndY=20.5877 EndZ=0
    g23: LineSegment StartX=-30.9254 StartY=20.5877 StartZ=0 EndX=-30.9254 EndY=17.4123 EndZ=0
    g24: LineSegment StartX=-30.9254 StartY=17.4123 StartZ=0 EndX=-28.1754 EndY=15.8246 EndZ=0
    g25: LineSegment StartX=-28.1754 StartY=15.8246 StartZ=0 EndX=-25.4254 EndY=17.4123 EndZ=0
    g26: LineSegment StartX=-25.4254 StartY=17.4123 StartZ=0 EndX=-25.4254 EndY=20.5877 EndZ=0
    g27: Circle CenterX=-28.1754 CenterY=19 CenterZ=0 NormalX=0 NormalY=0 NormalZ=1 AngleXU=0 Radius=3.17543
  constraints (64):
    c: Coincident(g0,g1)
    c: Coincident(g1,g2)
    c: Coincident(g2,g3)
    c: Coincident(g3,g4)
    c: Coincident(g4,g5)
    c: Coincident(g5,g0)
    c: Equal(g0, g1-g5) x5
    c: PointOnObject(g0,g6)
    c: PointOnObject(g1,g6)
    c: PointOnObject(g2,g6)
    c: PointOnObject(g3,g6)
    c: PointOnObject(g4,g6)
    c: PointOnObject(g5,g6)
    c: Coincident(g6,g-3)
    c: Coincident(g7,g8)
    c: Coincident(g8,g9)
    c: Coincident(g9,g10)
    c: Coincident(g10,g11)
    c: Coincident(g11,g12)
    c: Coincident(g12,g7)
    c: Equal(g7, g8-g12) x5
    c: PointOnObject(g7,g13)
    c: PointOnObject(g8,g13)
    c: PointOnObject(g9,g13)
    c: PointOnObject(g10,g13)
    c: PointOnObject(g11,g13)
    c: PointOnObject(g12,g13)
    c: Coincident(g13,g-4)
    c: Coincident(g14,g15)
    c: Coincident(g15,g16)
    c: Coincident(g16,g17)
    c: Coincident(g17,g18)
    c: Coincident(g18,g19)
    c: Coincident(g19,g14)
    c: Equal(g14, g15-g19) x5
    c: PointOnObject(g14,g20)
    c: PointOnObject(g15,g20)
    c: PointOnObject(g16,g20)
    c: PointOnObject(g17,g20)
    c: PointOnObject(g18,g20)
    c: PointOnObject(g19,g20)
    c: Coincident(g20,g-5)
    c: Coincident(g21,g22)
    c: Coincident(g22,g23)
    c: Coincident(g23,g24)
    c: Coincident(g24,g25)
    c: Coincident(g25,g26)
    c: Coincident(g26,g21)
    c: Equal(g21, g22-g26) x5
    c: PointOnObject(g21,g27)
    c: PointOnObject(g22,g27)
    c: PointOnObject(g23,g27)
    c: PointOnObject(g24,g27)
    c: PointOnObject(g25,g27)
    c: PointOnObject(g26,g27)
    c: Coincident(g27,g-6)
    c: Vertical(g5)
    c: Vertical(g9)
    c: Vertical(g19)
    c: Vertical(g23)
    c: DistanceX(g1,g0) = 5.5
    c: DistanceX(g8,g7) = 5.5
    c: DistanceX(g15,g14) = 5.5
    c: DistanceX(g22,g21) = 5.5
FEATURE [PartDesign::Pocket] Pocket008
  BaseFeature = -> Hole002
  Direction = (-0.965926,0.258819,1e-16)
  Length = 5
  Length2 = 5
  Profile = -> Sketch013
  ReferenceAxis = -> Sketch013 [N_Axis]
  Type = 0
FEATURE [Sketcher::SketchObject] Sketch014
  ExternalGeometry = -> [Pocket008]
  FullyConstrained = true
  MapMode = 5
  Placement = pos=(-39.653,10.625,0) rot=(-0.476905,0.621515,0.621515;4.0316rad)
  Support = -> [Pocket008]
  expr: Constraints[8] = Spreadsheet.interface_height + Spreadsheet.interface_clearance
  expr: Constraints[9] = Spreadsheet.interface_width + Spreadsheet.interface_clearance
  sketch-geometry (7):
    g0: LineSegment StartX=22.9254 StartY=79.25 StartZ=0 EndX=43.4254 EndY=79.25 EndZ=0
    g1: LineSegment StartX=43.4254 StartY=79.25 StartZ=0 EndX=43.4254 EndY=13.75 EndZ=0
    g2: LineSegment StartX=43.4254 StartY=13.75 StartZ=0 EndX=22.9254 EndY=13.75 EndZ=0
    g3: LineSegment StartX=22.9254 StartY=13.75 StartZ=0 EndX=22.9254 EndY=79.25 EndZ=0
    g4: LineSegment StartX=28.1754 StartY=74 StartZ=0 EndX=38.1754 EndY=19 EndZ=0
    g5: LineSegment StartX=38.1754 StartY=74 StartZ=0 EndX=28.1754 EndY=19 EndZ=0
    g6: GeomPoint X=33.1754 Y=46.5 Z=0
  constraints (17):
    c: Coincident(g0,g1)
    c: Coincident(g1,g2)
    c: Coincident(g2,g3)
    c: Coincident(g3,g0)
    c: Horizontal(g0)
    c: Horizontal(g2)
    c: Vertical(g1)
    c: Vertical(g3)
    c: DistanceX(g0,g0) = 20.5
    c: DistanceY(g3,g3) = 65.5
    c: Coincident(g4,g-3)
    c: Coincident(g4,g-6)
    c: Coincident(g5,g-4)
    c: Coincident(g5,g-5)
    c: PointOnObject(g6,g4)
    c: PointOnObject(g6,g5)
    c: Symmetric(g0,g1,g6)
FEATURE [PartDesign::Pocket] Pocket009
  BaseFeature = -> Pocket008
  Direction = (0.965926,-0.258819,-1e-16)
  Length = 2
  Length2 = 5
  Profile = -> Sketch014
  ReferenceAxis = -> Sketch014 [N_Axis]
  Type = 0
  expr: Length = Spreadsheet.walls_thickness
FEATURE [Sketcher::SketchObject] Sketch015
  ExternalGeometry = -> [Pocket009]
  FullyConstrained = true
  MapMode = 5
  Placement = pos=(0,0,0) rot=(1,0,0;3.14159rad)
  Support = -> [Pocket009]
  expr: Constraints[11] = Spreadsheet.pen_radius + Spreadsheet.pen_radius_tolerance
  expr: Constraints[15] = Spreadsheet.pen_hole_offset
  sketch-geometry (6):
    g0: LineSegment StartX=-32.0554 StartY=7.12153 StartZ=0 EndX=-43.5807 EndY=4.03334 EndZ=0
    g1: LineSegment StartX=-43.5807 StartY=4.03334 StartZ=0 EndX=-46.6689 EndY=15.5586 EndZ=0
    g2: LineSegment StartX=-46.6689 StartY=15.5586 StartZ=0 EndX=-35.1436 EndY=18.6468 EndZ=0
    g3: LineSegment StartX=-35.1436 StartY=18.6468 StartZ=0 EndX=-32.0554 EndY=7.12153 EndZ=0
    g4: Circle CenterX=-41.2611 CenterY=10.8313 CenterZ=0 NormalX=0 NormalY=0 NormalZ=1 AngleXU=0 Radius=2.7
    g5: LineSegment StartX=-45.1248 StartY=9.79598 StartZ=0 EndX=-41.2611 EndY=10.8313 EndZ=0
  constraints (16):
    c: Coincident(g0,g1)
    c: Coincident(g1,g2)
    c: Coincident(g2,g3)
    c: Coincident(g3,g0)
    c: Coincident(g0,g-4)
    c: PointOnObject(g2,g-3)
    c: PointOnObject(g0,g-6)
    c: PointOnObject(g0,g-4)
    c: PointOnObject(g1,g-6)
    c: Equal(g0,g3)
    c: Equal(g0,g1)
    c: Radius(g4) = 2.7
    c: Coincident(g5,g4)
    c: Perpendicular(g5,g1)
    c: Symmetric(g1,g0,g5)
    c: Distance(g5) = 4
FEATURE [PartDesign::Pocket] Pocket010
  BaseFeature = -> Pocket009
  Direction = (0,0,1)
  Length = 93
  Length2 = 5
  Profile = -> Sketch015
  ReferenceAxis = -> Sketch015 [N_Axis]
  Type = 0
  expr: Length = Spreadsheet.main_case_width - Spreadsheet.walls_thickness
FEATURE [Sketcher::SketchObject] Sketch016
  ExternalGeometry = -> [Pocket010]
  FullyConstrained = true
  MapMode = 5
  Placement = pos=(0,0,0) rot=(1,0,0;3.14159rad)
  Support = -> [Pocket010]
  sketch-geometry (4):
    g0: LineSegment StartX=-40.5623 StartY=8.22326 StartZ=0 EndX=-44.426 EndY=7.18798 EndZ=0
    g1: LineSegment StartX=-44.426 StartY=7.18798 StartZ=0 EndX=-45.8236 EndY=12.404 EndZ=0
    g2: LineSegment StartX=-45.8236 StartY=12.404 StartZ=0 EndX=-41.9599 EndY=13.4393 EndZ=0
    g3: LineSegment StartX=-41.9599 StartY=13.4393 StartZ=0 EndX=-40.5623 EndY=8.22326 EndZ=0
  constraints (12):
    c: Coincident(g0,g1)
    c: Coincident(g1,g2)
    c: Coincident(g2,g3)
    c: Coincident(g3,g0)
    c: PointOnObject(g0,g-4)
    c: PointOnObject(g1,g-4)
    c: PointOnObject(g2,g-3)
    c: PointOnObject(g0,g-3)
    c: PointOnObject(g-3,g3)
    c: Parallel(g3,g1)
    c: Parallel(g2,g0)
    c: Perpendicular(g2,g1)
FEATURE [PartDesign::Pocket] Pocket011
  BaseFeature = -> Pocket010
  Direction = (0,0,1)
  Length = 11.5
  Length2 = 5
  Profile = -> Sketch016
  ReferenceAxis = -> Sketch016 [N_Axis]
  Type = 0
  expr: Length = Spreadsheet.pen_grip_height
FEATURE [PartDesign::CoordinateSystem] LCS_interface
  AttacherType = Attacher::AttachEngine3D
  MapMode = 11
  Placement = pos=(-45.0135,-17.108,74) rot=(-0.476905,0.621515,0.621515;4.0316rad)
  Support = -> [Pocket011]
FEATURE [Sketcher::SketchObject] Sketch017
  ExternalGeometry = -> [Pocket011]
  FullyConstrained = true
  MapMode = 5
  Placement = pos=(-39.653,10.625,0) rot=(-0.476905,0.621515,0.621515;4.0316rad)
  Support = -> [Pocket011]
  sketch-geometry (2):
    g0: Circle CenterX=-24.8246 CenterY=86.95 CenterZ=0 NormalX=0 NormalY=0 NormalZ=1 AngleXU=0 Radius=1.05
    g1: Circle CenterX=40.1754 CenterY=86.95 CenterZ=0 NormalX=0 NormalY=0 NormalZ=1 AngleXU=0 Radius=1.05
  constraints (4):
    c: Symmetric(g-5,g-6,g0)
    c: Symmetric(g-9,g-10,g1)
    c: Tangent(g0,g-5)
    c: Tangent(g1,g-9)
FEATURE [PartDesign::Pocket] Pocket012
  BaseFeature = -> Pocket011
  Direction = (0.965926,-0.258819,-1e-16)
  Length = 2
  Length2 = 5
  Profile = -> Sketch017
  ReferenceAxis = -> Sketch017 [N_Axis]
  Type = 3
  UpToFace = -> Pocket011 [Face67]
  expr: Length = Spreadsheet.walls_thickness
FEATURE [Sketcher::SketchObject] Sketch018
  ExternalGeometry = -> [Pocket012]
  FullyConstrained = true
  MapMode = 5
  Placement = pos=(39.653,-10.625,0) rot=(0.677661,0.519988,0.519988;1.95044rad)
  Support = -> [Pocket012]
  sketch-geometry (2):
    g0: Circle CenterX=-19.2111 CenterY=86.95 CenterZ=0 NormalX=0 NormalY=0 NormalZ=1 AngleXU=0 Radius=1.05
    g1: Circle CenterX=25.7889 CenterY=86.95 CenterZ=0 NormalX=0 NormalY=0 NormalZ=1 AngleXU=0 Radius=1.05
  constraints (4):
    c: Symmetric(g-4,g-6,g0)
    c: Symmetric(g-8,g-10,g1)
    c: Tangent(g0,g-5)
    c: Tangent(g1,g-9)
FEATURE [PartDesign::Pocket] Pocket013
  BaseFeature = -> Pocket012
  Direction = (-0.965926,0.258819,-2e-16)
  Length = 0
  Length2 = 5
  Profile = -> Sketch018
  ReferenceAxis = -> Sketch018 [N_Axis]
  Type = 3
  UpToFace = -> Pocket012 [Face80]
FEATURE [PartDesign::Body] Body  label="Körper"
  Group = -> [Sketch,Pad,Sketch001,Pocket,Sketch002,Pocket001,Sketch003,Pocket002,Fillet,Sketch004,Hole,Sketch005,Pocket003,Sketch006,Pocket004,Sketch007,Pad001,Sketch008,Hole001,Sketch009,Pocket005,Sketch010,Pocket006,Sketch011,Pocket007,Sketch012,Hole002,Sketch013,Pocket008,Sketch014,Pocket009,Sketch015,Pocket010,Sketch016,Pocket011,Sketch017,Pocket012,Sketch018,Pocket013]
  Origin = -> Origin
  Tip = -> Pocket013
FEATURE [App::Part] Model
  AssemblyType = Part::Link
  Group = -> [LCS_Origin,Constraints,Variables,Configurations,Body,LCS_MLX,LCS_Raspi,LCS_Display,LCS_beam,LCS_interface]
  Origin = -> Origin001
  Type = Assembly
FEATURE [Mesh::Feature] Mesh  label="Körper (Meshed)"
